# Revit family: Takbasket sammansatt
name_source: partatom
category: Generic Models
revit_build: Autodesk Revit 2017 (Build: 20160225_1515(x64)
units: mm (PartAtom-declared; Revit-internal decimal feet)

## family parameters
Always vertical = Yes
Can host rebar = No
Cut with Voids When Loaded = No
Part Type = Normal
Room Calculation Point = No
Round Connector Dimension = Use Diameter
Shared = No
Work Plane-Based = No

## types (1)
- Takbasket sammansatt
    Angle_C2 = 45.00°
    B1 = 3752 mm
    Beam_offset = 3000 mm  [stored 9.84252 ft]
    C1 = 2885 mm
    C1_horizontal_start = 5913 mm
    C1_vertical_start = 1373 mm
    C2 = 2633 mm
    Height = 8000 mm  [stored 26.2467 ft]
    Height_vertical = 4932 mm
    Manufacturer = Saxi Vägg AB
    Model = Takbasket
    URL = www.saxi.se
    folded_b1 = 3422 mm  [stored 11.227 ft]
    folded_b2 = 699 mm
    length_beam = 10000 mm  [stored 32.8084 ft]

note: [stored X ft] marks values corroborated as IEEE doubles in the binary element streams (Revit-internal decimal feet)

## geometry (parser evidence)
native form markers: Sweep x59
no freeform markers — native parametric forms only
